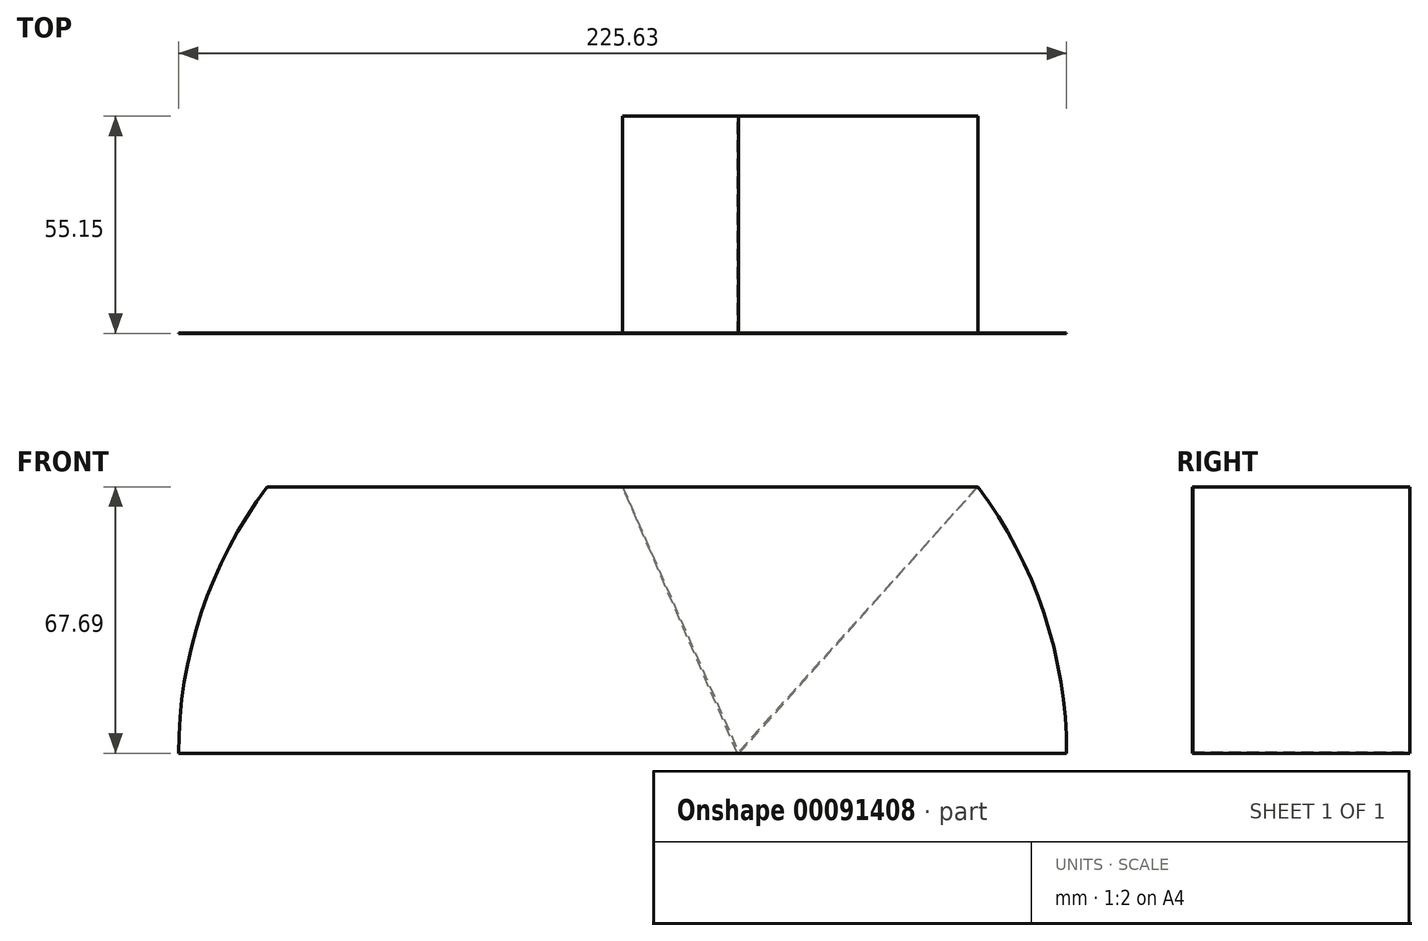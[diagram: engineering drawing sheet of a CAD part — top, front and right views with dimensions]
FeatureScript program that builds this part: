
annotation { "Feature Type Name" : "Feature", "Feature Type Description" : "" }
export const myFeature = defineFeature(function(context is Context, id is Id, definition is map)
    precondition{}
    {
        {
            var Q0;
            Q0=qCreatedBy(makeId("Front.planeOp"),FACE);
            var sketch = newSketch(context, id + "F0", { "sketchPlane" : qUnion([Q0])});
            skLineSegment(sketch, "E0", {"start": v(-115.26, -73.32) * mm, "end": v(113.39, -73.32) * mm});
            skArc(sketch, "E1", {"start": v(-91.19, -5.63) * mm, "mid": v(-107.96, -37.64) * mm, "end": v(-113.75, -73.32) * mm});
            skLineSegment(sketch, "E2", {"start": v(-91.19, -5.63) * mm, "end": v(89.32, -5.63) * mm});
            skArc(sketch, "E3.trimOffspring", {"start": v(111.88, -73.32) * mm, "mid": v(106.1, -37.64) * mm, "end": v(89.32, -5.63) * mm});
            skLineSegment(sketch, "E4", {"start": v(-91.19, -5.63) * mm, "end": v(-30.1, -73.32) * mm});
            skLineSegment(sketch, "E5", {"start": v(-30.1, -73.32) * mm, "end": v(-0.93, -5.63) * mm});
            skLineSegment(sketch, "E6", {"start": v(-0.93, -5.63) * mm, "end": v(28.7, -73.32) * mm});
            skLineSegment(sketch, "E7", {"start": v(28.7, -73.32) * mm, "end": v(89.32, -5.63) * mm});
            skLineSegment(sketch, "E8.MirrorCS", {"start": v(28.23, -73.32) * mm, "end": v(-0.93, -5.63) * mm});
            skLineSegment(sketch, "E9.MirrorCS", {"start": v(89.32, -5.63) * mm, "end": v(-91.19, -5.63) * mm});
            skLineSegment(sketch, "E10.MirrorCS", {"start": v(89.32, -5.63) * mm, "end": v(28.23, -73.32) * mm});
            skArc(sketch, "E11.MirrorCS", {"start": v(89.32, -5.63) * mm, "mid": v(106.1, -37.64) * mm, "end": v(111.88, -73.32) * mm});
            skLineSegment(sketch, "E12.MirrorCS", {"start": v(113.39, -73.32) * mm, "end": v(-115.26, -73.32) * mm});
            skSolve(sketch);
        }
        {
            var Q0;
            Q0 = qSketchRegion(id + "F0", true);
            extrude(context, id + "F1", {"entities" : qUnion([Q0]), "depth" : 55.15 * mm});
        }
        {
            var Q0;
            {var subQ0=sQuery(id+"F0.wireOp",EDGE,"E1");Q0=makeQuery(id+"F0.imprint","IMPRINT",FACE,{"disambiguationData":[TD([[makeQuery(id+"F0.imprint","IMPRINT",EDGE,{"derivedFrom":subQ0}),1.0]])]});}
            var Q1;
            {var subQ0=sQuery(id+"F0.wireOp",EDGE,"E4");Q1=makeQuery(id+"F0.imprint","IMPRINT",FACE,{"disambiguationData":[TD([[makeQuery(id+"F0.imprint","IMPRINT",EDGE,{"derivedFrom":subQ0}),1.0]])]});}
            var Q2;
            {var subQ0=sQuery(id+"F0.wireOp",EDGE,"E5");Q2=makeQuery(id+"F0.imprint","IMPRINT",FACE,{"disambiguationData":[TD([[makeQuery(id+"F0.imprint","IMPRINT",EDGE,{"derivedFrom":subQ0}),-1.0]])]});}
            var Q3;
            {var subQ1=sQuery(id+"F0.wireOp",EDGE,"E6");var subQ3=sQuery(id+"F0.wireOp",EDGE,"E10.MirrorCS");var subQ4=makeQuery(id+"F0.imprint","INTERSECT",VERTEX,{"derivedFrom":[subQ1,subQ3]});Q3=makeQuery(id+"F0.imprint","IMPRINT",FACE,{"disambiguationData":[TD([[makeQuery(id+"F0.imprint","IMPRINT",EDGE,{"disambiguationData":[TD([[subQ4,1.0]])],"derivedFrom":subQ1}),1.0]])]});}
            var Q4;
            {var subQ0=sQuery(id+"F0.wireOp",EDGE,"E7");Q4=makeQuery(id+"F0.imprint","IMPRINT",FACE,{"disambiguationData":[TD([[makeQuery(id+"F0.imprint","IMPRINT",EDGE,{"derivedFrom":subQ0}),-1.0]])]});}
            extrude(context, id + "F2", {"entities" : qUnion([Q0, Q1, Q2, Q3, Q4]), "operationType" : NewBodyOperationType.REMOVE, "depth" : 55.1 * mm});
        }
    });
